# Revit family: Prises non verrouilllées 380_415 V
name_source: partatom
category: Installations électriques
revit_build: Autodesk Revit 2018 (Build: 20170223_1515(x64)
units: mm (PartAtom-declared; Revit-internal decimal feet)

## family parameters
Conserver l'orientation des annotations = Non
Cote de connecteur circulaire = Utiliser le diamètre
Couper avec des vides une fois chargée = Non
Hôte = Face
Partagée = Non
Point de calcul de pièce = Non
Type d'élément = Normal

## types (21) — shared parameters
Couleur caractéristique = rouge
Elévation par défaut = 1000 mm  [stored 3.28084 ft]
Fabricant = Legrand
Famille produit = 0854-P17 TEMPRA PRO
Position de la Terre h = 6
Prise au standard international pour montage encastré ou saillie avec accessoire permet la connexion d'appareils de puissance = Prise au standard international pour montage encastré ou saillie avec accessoire permet la connexion d'appareils de puissance
Standard CEI ou NFC = CEI
Température maximum d'utilisation = 40
Température minimum d'utilisation = -25
Tension V = 400 V  50/60 Hz  rouge
matériau du boitier = plastique
résistance aux chocs IK = 9
type de raccordement = bornes à vis

## per-type parameters (varying)
| type | Description | Intensité A | Nombre de pôles | Température minimum d'installation | classe de protection IP | entraxe de fixation horizontal mm | entraxe de fixation vertical mm | hauteur mm | installation Encastrée E ou Saillie S | largeur mm | profondeur d'encastrement mm | profondeur mm | sans halogène |
| P17 Pro - IP66/67 - 63 A - 3P+N+T | LG-555589_Panneau de montage prise P17 Pro - IP66/67 - 380/415 V - 63 A - 3P+N+T | 63 A | 5 | -5 |  | 77 mm  [stored 0.252625 ft] | 85 mm | 106 mm  [stored 0.347769 ft] | encastré | 106 mm  [stored 0.347769 ft] | 84 mm  [stored 0.275591 ft] | 161 mm  [stored 0.528215 ft] | Non |
| P17 Pro - IP66/67 - 63 A - 3P+T | LG-555588_Panneau de montage prise P17 Pro - IP66/67 - 380/415 V - 63 A - 3P+T | 63 A | 4 | -5 |  | 77 mm  [stored 0.252625 ft] | 85 mm | 106 mm  [stored 0.347769 ft] | encastré | 106 mm  [stored 0.347769 ft] | 84 mm  [stored 0.275591 ft] | 161 mm  [stored 0.528215 ft] | Non |
| P17 Pro - IP66/67 - 125 A - 3P+N+T | LG-555689_Panneau de montage prise P17 Pro - IP66/67 - 380/415 V - 125 A - 3P+N+T | 125 A | 5 | -5 |  | 124 mm | 124 mm | 146 mm  [stored 0.479003 ft] | encastré | 146 mm  [stored 0.479003 ft] | 89 mm  [stored 0.291995 ft] | 182 mm | Non |
| P17 Pro - IP66/67 - 125 A - 3P+T | LG-555688_Panneau de montage prise P17 Pro - IP66/67 - 380/415 V - 125 A - 3P+T | 125 A | 4 | -5 |  | 124 mm | 124 mm | 146 mm  [stored 0.479003 ft] | encastré | 146 mm  [stored 0.479003 ft] | 89 mm  [stored 0.291995 ft] | 182 mm | Non |
| P17 - IP66/67 - 32 A - 3P+N+T | LG-555489_Panneau de montage prise P17 - IP66/67 - 380/415 V - 32 A - 3P+N+T | 32 A | 5 | -5 |  | 70 mm  [stored 0.229659 ft] | 70 mm  [stored 0.229659 ft] | 84 mm  [stored 0.275591 ft] | encastré et saillie | 84 mm  [stored 0.275591 ft] | 43 mm  [stored 0.141076 ft] | 94 mm  [stored 0.308399 ft] | Non |
| P17 - IP66/67 - 32 A - 3P+T | LG-555488_Panneau de montage prise P17 - IP66/67 - 380/415 V - 32 A - 3P+T | 32 A | 4 | -5 |  | 70 mm  [stored 0.229659 ft] | 70 mm  [stored 0.229659 ft] | 84 mm  [stored 0.275591 ft] | encastré et saillie | 84 mm  [stored 0.275591 ft] | 42 mm | 92 mm | Non |
| P17 - IP66/67 - 16 A - 3P+N+T | LG-555389_Panneau de montage prise P17 - IP66/67 - 380/415 V - 16 A - 3P+N+T | 16 A | 5 | -5 |  | 70 mm  [stored 0.229659 ft] | 70 mm  [stored 0.229659 ft] | 84 mm  [stored 0.275591 ft] | encastré et saillie | 84 mm  [stored 0.275591 ft] | 37 mm  [stored 0.121391 ft] | 81 mm | Non |
| P17 - IP66/67 - 16 A - 3P+T | LG-555388_Panneau de montage prise P17 - IP66/67 - 380/415 V - 16 A - 3P+T | 16 A | 4 | -5 |  | 70 mm  [stored 0.229659 ft] | 70 mm  [stored 0.229659 ft] | 84 mm  [stored 0.275591 ft] | encastré et saillie | 84 mm  [stored 0.275591 ft] | 36 mm | 79 mm | Non |
| P17 - 32A - 3P+T - IP1 | LG-555290_Panneau de montage prise P17  32A 3P+T 440/460V IP44 | 32 A | 4 | -5 | IP44 | 70 mm  [stored 0.229659 ft] | 70 mm  [stored 0.229659 ft] | 84 mm  [stored 0.275591 ft] | encastré et saillie | 84 mm  [stored 0.275591 ft] | 42 mm | 87 mm | Oui |
| P17 - IP44 - 32 A - 3P+N+T | LG-555289_Panneau de montage prise P17 - sortie inclinée - IP44 - 380/415 V - 32 A - 3P+N+T | 32 A | 5 | -5 | IP44 | 70 mm  [stored 0.229659 ft] | 70 mm  [stored 0.229659 ft] | 84 mm  [stored 0.275591 ft] | encastré et saillie | 84 mm  [stored 0.275591 ft] | 43 mm  [stored 0.141076 ft] | 89 mm  [stored 0.291995 ft] | Oui |
| P17 - IP44 - 32 A - 3P+T | LG-555288_Panneau de montage prise P17 - sortie inclinée - IP44 - 380/415 V - 32 A - 3P+T | 32 A | 4 | -5 | IP44 | 70 mm  [stored 0.229659 ft] | 70 mm  [stored 0.229659 ft] | 84 mm  [stored 0.275591 ft] | encastré et saillie | 84 mm  [stored 0.275591 ft] | 42 mm | 87 mm | Oui |
| P17 - IP44 - 16A - 3P+N+T 1 | LG-555189_Panneau de montage prise P17 - sortie inclinée - IP44 - 380/415 V - 16 A - 3P+N+T | 16 A | 5 | -5 | IP44 | 70 mm  [stored 0.229659 ft] | 70 mm  [stored 0.229659 ft] | 84 mm  [stored 0.275591 ft] | encastré et saillie | 84 mm  [stored 0.275591 ft] | 37 mm  [stored 0.121391 ft] | 76 mm | Oui |
| P17 - IP44 - 16A - 3P+T 1 | LG-555188_Panneau de montage prise P17 - sortie inclinée - IP44 - 380/415 V - 16 A - 3P+T | 16 A | 4 | -5 | IP44 | 70 mm  [stored 0.229659 ft] | 70 mm  [stored 0.229659 ft] | 84 mm  [stored 0.275591 ft] | encastré et saillie | 84 mm  [stored 0.275591 ft] | 36 mm | 74 mm  [stored 0.242782 ft] | Oui |
| P17 - 32A - 4P+T - IP44 | LG-090166_Panneau de montage prise P17  32A 4P+T 380/415V IP44 | 32 A | 5 | -5 | IP44 | 70 mm  [stored 0.229659 ft] | 70 mm  [stored 0.229659 ft] | 84 mm  [stored 0.275591 ft] | encastré et saillie | 84 mm  [stored 0.275591 ft] | 43 mm  [stored 0.141076 ft] | 89 mm  [stored 0.291995 ft] | Oui |
| P17 - 32A - 3P+T - IP44 | LG-090165_Panneau de montage prise P17  32A 3P+T 380/415V IP44 | 32 A | 4 | -5 | IP44 | 70 mm  [stored 0.229659 ft] | 70 mm  [stored 0.229659 ft] | 84 mm  [stored 0.275591 ft] | encastré et saillie | 84 mm  [stored 0.275591 ft] | 42 mm | 87 mm | Oui |
| P17 - 16A - 4P+T - IP44 | LG-090164_Panneau de montage prise P17  16A 4P+T 380/415V IP44 | 16 A | 5 | -5 | IP44 | 70 mm  [stored 0.229659 ft] | 70 mm  [stored 0.229659 ft] | 84 mm  [stored 0.275591 ft] | encastré et saillie | 84 mm  [stored 0.275591 ft] | 37 mm  [stored 0.121391 ft] | 76 mm | Oui |
| P17 - 16A - 3P+T - IP44 | LG-090163_Panneau de montage prise P17  16A 3P+T 380/415V IP44 | 16 A | 4 | -5 | IP44 | 70 mm  [stored 0.229659 ft] | 70 mm  [stored 0.229659 ft] | 84 mm  [stored 0.275591 ft] | encastré et saillie | 84 mm  [stored 0.275591 ft] | 36 mm | 74 mm  [stored 0.242782 ft] | Oui |
| P17 - IP44 - 32A - 3P+N+T | LG-058059_Panneau de montage prise P17  - IP44 - sortie droite - 380/415 V - 32 A -3P+N+T | 32 A | 4 |  | IP44 | 60 mm | 60 mm | 105 mm | encastré | 77 mm  [stored 0.252625 ft] | 31 mm | 93 mm | Oui |
| P17 - IP44 - 32A - 3P+T | LG-058058_Panneau de montage prise P17  - IP44 - sortie droite - 380/415 V - 32 A -3P+T | 32 A | 3 |  | IP44 | 60 mm | 60 mm | 98 mm | encastré | 75 mm  [stored 0.246063 ft] | 31 mm | 93 mm | Oui |
| P17 - IP44 - 16A - 3P+N+T | LG-057359_Panneau de montage prise P17 - IP44 - 380/415 V - 16 A - 3P+N+T | 16 A | 4 |  | IP44 | 52 mm | 52 mm | 94 mm  [stored 0.308399 ft] | encastré | 70 mm  [stored 0.229659 ft] | 22 mm  [stored 0.0721785 ft] | 73 mm | Oui |
| P17 - IP44 - 16A - 3P+T | LG-057358_Panneau de montage prise P17 - IP44 - 380/415 V - 16 A - 3P+T | 16 A | 3 |  | IP44 | 52 mm | 52 mm | 86 mm | encastré | 65 mm  [stored 0.213255 ft] | 22 mm  [stored 0.0721785 ft] | 73 mm | Oui |

note: [stored X ft] marks values corroborated as IEEE doubles in the binary element streams (Revit-internal decimal feet)
